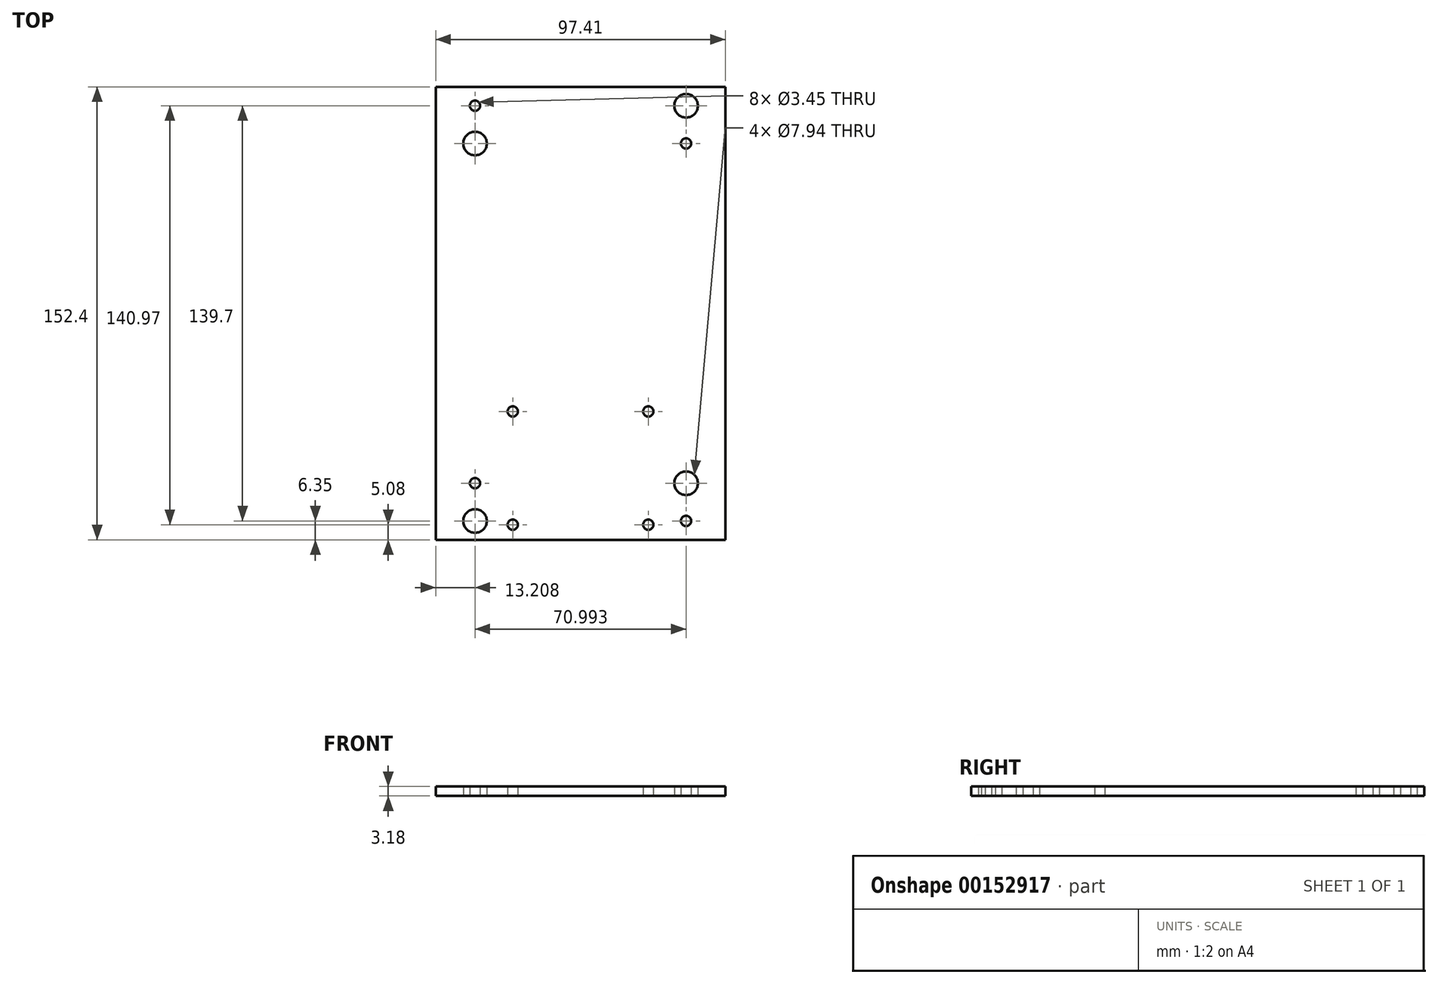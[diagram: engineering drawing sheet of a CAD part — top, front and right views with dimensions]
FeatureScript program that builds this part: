
annotation { "Feature Type Name" : "Feature", "Feature Type Description" : "" }
export const myFeature = defineFeature(function(context is Context, id is Id, definition is map)
    precondition{}
    {
        {
            var Q0;
            Q0=qCreatedBy(makeId("Top.planeOp"),FACE);
            var sketch = newSketch(context, id + "F0", { "sketchPlane" : qUnion([Q0])});
            skLineSegment(sketch, "E0.bottom", {"start": v(0, 0) * mm, "end": v(97.4, 0) * mm});
            skLineSegment(sketch, "E0.top", {"start": v(0, -152.4) * mm, "end": v(97.4, -152.4) * mm});
            skLineSegment(sketch, "E0.left", {"start": v(0, 0) * mm, "end": v(0, -152.4) * mm});
            skLineSegment(sketch, "E0.right", {"start": v(97.4, 0) * mm, "end": v(97.4, -152.4) * mm});
            skLineSegment(sketch, "E1", {"start": v(13.2, 0) * mm, "end": v(13.2, -6.35) * mm, "construction": true});
            skLineSegment(sketch, "E2", {"start": v(13.2, -6.35) * mm, "end": v(0, -6.35) * mm, "construction": true});
            skCircle(sketch, "E3", {"center": v(13.2, -6.35) * mm, "radius": 1.73 * mm});
            skLineSegment(sketch, "E4", {"start": v(13.2, -6.35) * mm, "end": v(13.2, -19.05) * mm, "construction": true});
            skCircle(sketch, "E5", {"center": v(13.2, -19.05) * mm, "radius": 3.97 * mm});
            skLineSegment(sketch, "E6", {"start": v(13.2, -152.4) * mm, "end": v(13.2, -146.05) * mm, "construction": true});
            skLineSegment(sketch, "E7", {"start": v(13.2, -146.05) * mm, "end": v(13.2, -133.35) * mm, "construction": true});
            skCircle(sketch, "E8", {"center": v(13.2, -133.35) * mm, "radius": 1.73 * mm});
            skCircle(sketch, "E9", {"center": v(13.2, -146.05) * mm, "radius": 3.97 * mm});
            skLineSegment(sketch, "E10", {"start": v(97.4, -6.35) * mm, "end": v(84.2, -6.35) * mm, "construction": true});
            skLineSegment(sketch, "E11", {"start": v(84.2, -6.35) * mm, "end": v(84.2, 0) * mm, "construction": true});
            skLineSegment(sketch, "E12", {"start": v(84.2, -6.35) * mm, "end": v(84.2, -19.05) * mm, "construction": true});
            skLineSegment(sketch, "E13", {"start": v(84.2, -152.4) * mm, "end": v(84.2, -146.05) * mm, "construction": true});
            skLineSegment(sketch, "E14", {"start": v(84.2, -146.05) * mm, "end": v(84.2, -133.35) * mm, "construction": true});
            skCircle(sketch, "E15", {"center": v(84.2, -6.35) * mm, "radius": 3.97 * mm});
            skCircle(sketch, "E16", {"center": v(84.2, -19.05) * mm, "radius": 1.73 * mm});
            skCircle(sketch, "E17", {"center": v(84.2, -133.35) * mm, "radius": 3.97 * mm});
            skCircle(sketch, "E18", {"center": v(84.2, -146.05) * mm, "radius": 1.73 * mm});
            skLineSegment(sketch, "E19", {"start": v(71.5, -152.4) * mm, "end": v(71.5, -147.32) * mm, "construction": true});
            skLineSegment(sketch, "E20", {"start": v(71.5, -147.32) * mm, "end": v(71.5, -109.22) * mm, "construction": true});
            skLineSegment(sketch, "E21", {"start": v(84.2, -146.05) * mm, "end": v(77.85, -146.05) * mm, "construction": true});
            skLineSegment(sketch, "E22", {"start": v(77.85, -146.05) * mm, "end": v(77.85, -147.32) * mm, "construction": true});
            skLineSegment(sketch, "E23", {"start": v(77.85, -147.32) * mm, "end": v(71.5, -147.32) * mm, "construction": true});
            skLineSegment(sketch, "E24", {"start": v(25.9, -152.4) * mm, "end": v(25.9, -147.32) * mm, "construction": true});
            skLineSegment(sketch, "E25", {"start": v(25.9, -147.32) * mm, "end": v(25.9, -109.22) * mm, "construction": true});
            skLineSegment(sketch, "E26", {"start": v(13.2, -146.05) * mm, "end": v(19.56, -146.05) * mm, "construction": true});
            skLineSegment(sketch, "E27", {"start": v(19.56, -147.32) * mm, "end": v(19.56, -146.05) * mm, "construction": true});
            skLineSegment(sketch, "E28", {"start": v(19.56, -147.32) * mm, "end": v(25.9, -147.32) * mm, "construction": true});
            skCircle(sketch, "E29", {"center": v(25.9, -109.22) * mm, "radius": 1.73 * mm});
            skCircle(sketch, "E30", {"center": v(71.5, -109.22) * mm, "radius": 1.73 * mm});
            skCircle(sketch, "E31", {"center": v(71.5, -147.32) * mm, "radius": 1.73 * mm});
            skCircle(sketch, "E32", {"center": v(25.9, -147.32) * mm, "radius": 1.73 * mm});
            skSolve(sketch);
        }
        {
            var Q0;
            Q0=makeQuery(id+"F0.imprint","IMPRINT",FACE,{"disambiguationData":[TD([[makeQuery(id+"F0.imprint","IMPRINT",EDGE,{"derivedFrom":sQuery(id+"F0.wireOp",EDGE,"E0.bottom")}),-1.0]])]});
            extrude(context, id + "F1", {"entities" : qUnion([Q0]), "depth" : 3.17 * mm});
        }
    });
